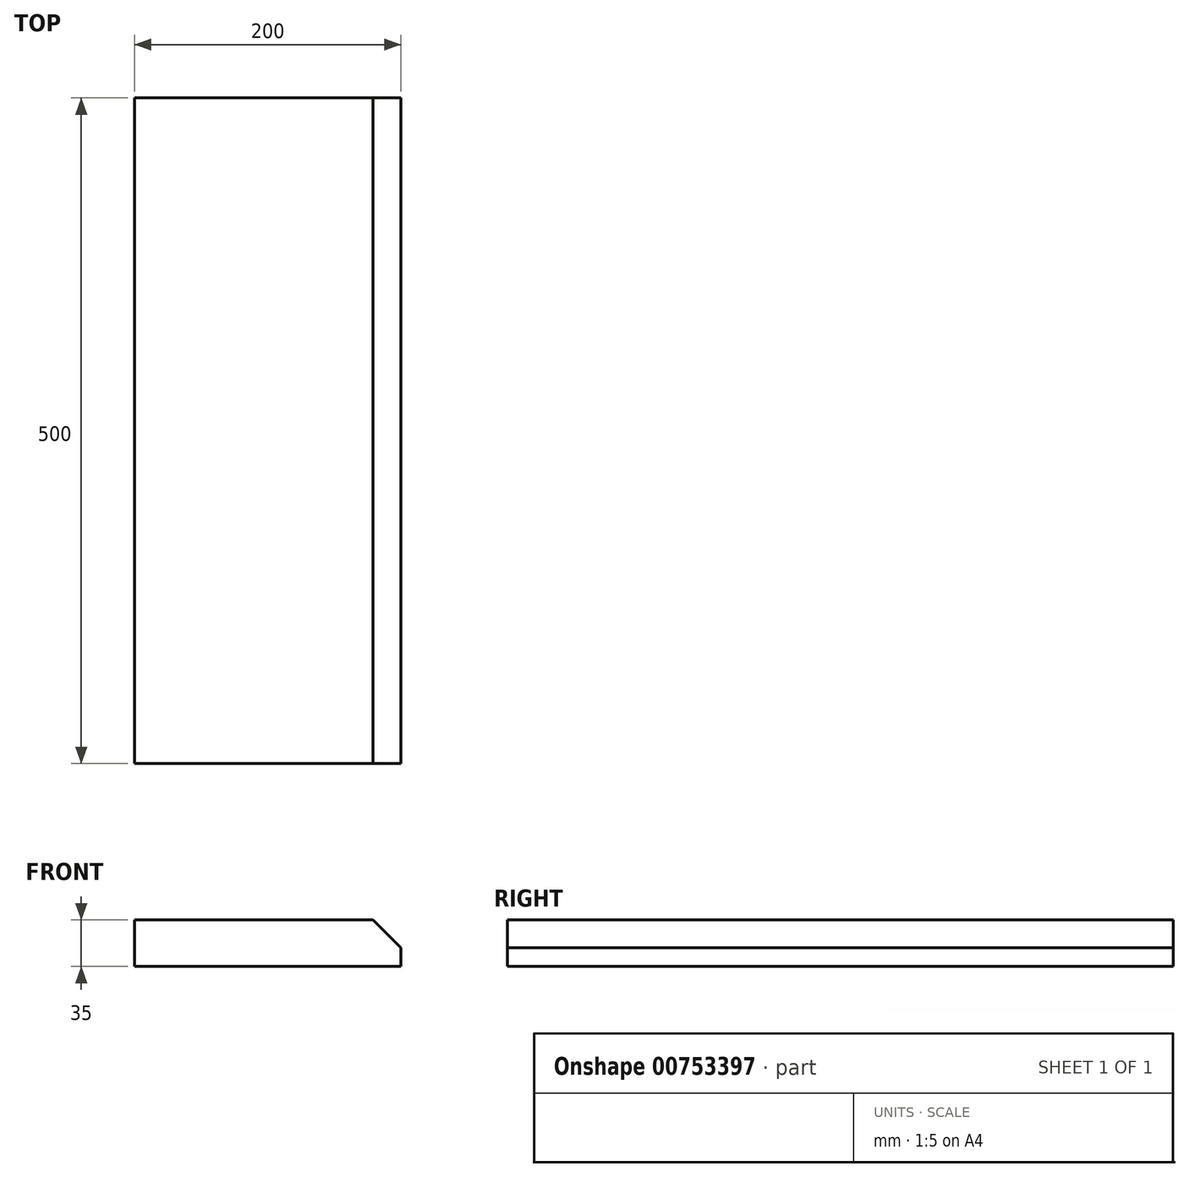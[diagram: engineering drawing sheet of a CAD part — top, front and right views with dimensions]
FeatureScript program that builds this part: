
annotation { "Feature Type Name" : "Feature", "Feature Type Description" : "" }
export const myFeature = defineFeature(function(context is Context, id is Id, definition is map)
    precondition{}
    {
        {
            var Q0;
            Q0=qCreatedBy(makeId("Front.planeOp"),FACE);
            var sketch = newSketch(context, id + "F0", { "sketchPlane" : qUnion([Q0])});
            skLineSegment(sketch, "E0", {"start": v(0, 0) * mm, "end": v(200, 0) * mm});
            skLineSegment(sketch, "E1", {"start": v(200, 0) * mm, "end": v(200, 14) * mm});
            skLineSegment(sketch, "E2", {"start": v(200, 14) * mm, "end": v(179, 35) * mm});
            skLineSegment(sketch, "E3", {"start": v(179, 35) * mm, "end": v(0, 35) * mm});
            skLineSegment(sketch, "E4", {"start": v(0, 35) * mm, "end": v(0, 0) * mm});
            skSolve(sketch);
        }
        {
            var Q0;
            Q0 = qSketchRegion(id + "F0", true);
            extrude(context, id + "F1", {"entities" : qUnion([Q0]), "endBound" : BoundingType.SYMMETRIC, "depth" : 500 * mm, "offsetDistance" : 25 * mm});
        }
    });
